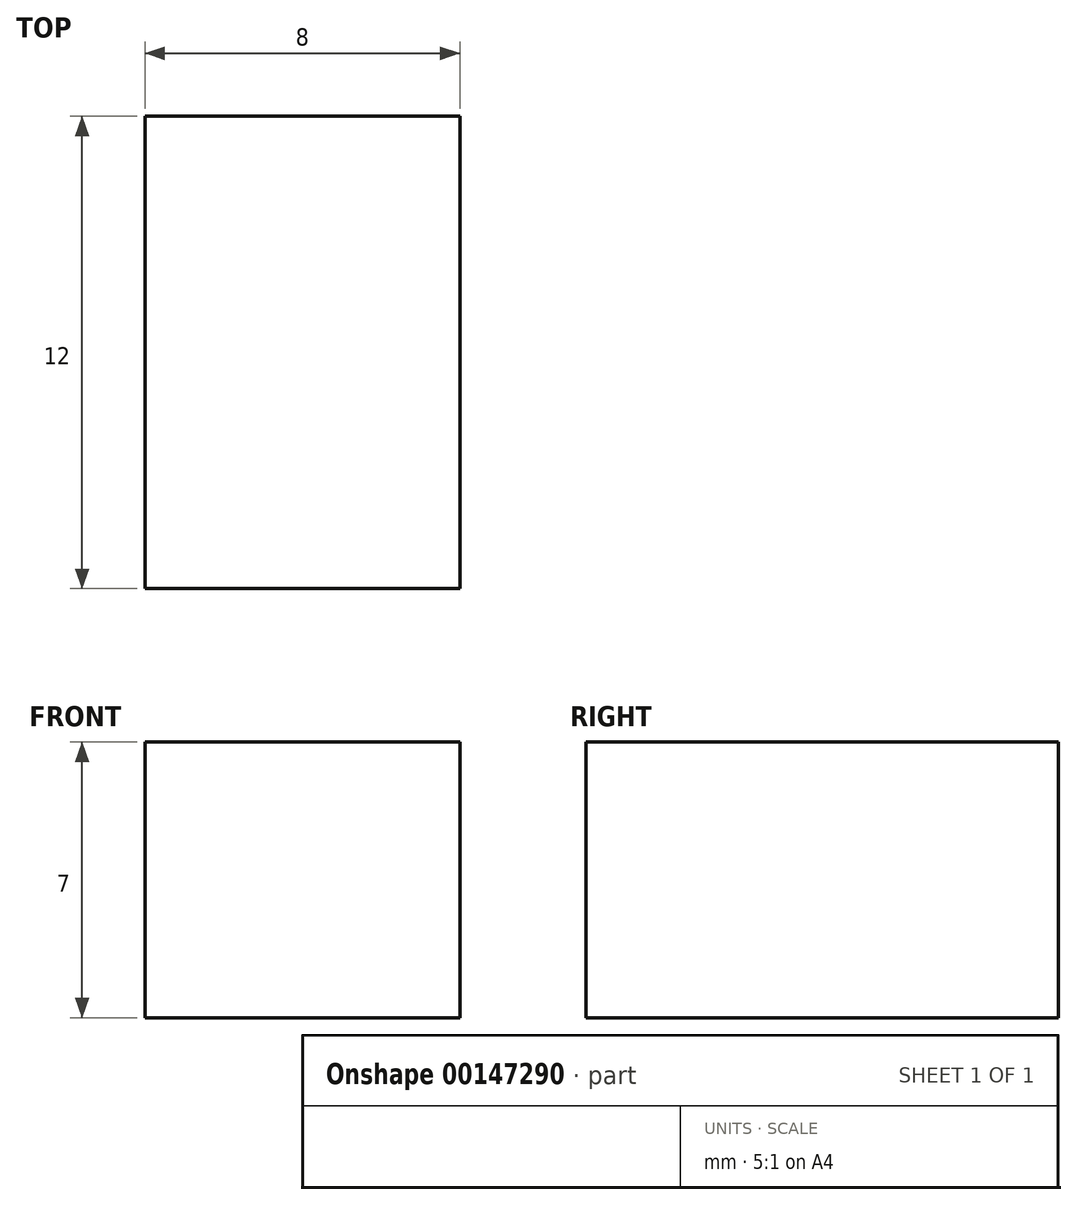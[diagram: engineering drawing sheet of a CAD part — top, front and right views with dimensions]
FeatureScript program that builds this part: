
annotation { "Feature Type Name" : "Feature", "Feature Type Description" : "" }
export const myFeature = defineFeature(function(context is Context, id is Id, definition is map)
    precondition{}
    {
        {
            var Q0;
            Q0=qCreatedBy(makeId("Front.planeOp"),FACE);
            var sketch = newSketch(context, id + "F0", { "sketchPlane" : qUnion([Q0])});
            skLineSegment(sketch, "E0.bottom", {"start": v(0, 0) * mm, "end": v(8, 0) * mm});
            skLineSegment(sketch, "E0.top", {"start": v(0, 7) * mm, "end": v(8, 7) * mm});
            skLineSegment(sketch, "E0.left", {"start": v(0, 0) * mm, "end": v(0, 7) * mm});
            skLineSegment(sketch, "E0.right", {"start": v(8, 0) * mm, "end": v(8, 7) * mm});
            skSolve(sketch);
        }
        {
            var Q0;
            Q0 = qSketchRegion(id + "F0", true);
            extrude(context, id + "F1", {"entities" : qUnion([Q0]), "depth" : 12 * mm});
        }
    });
